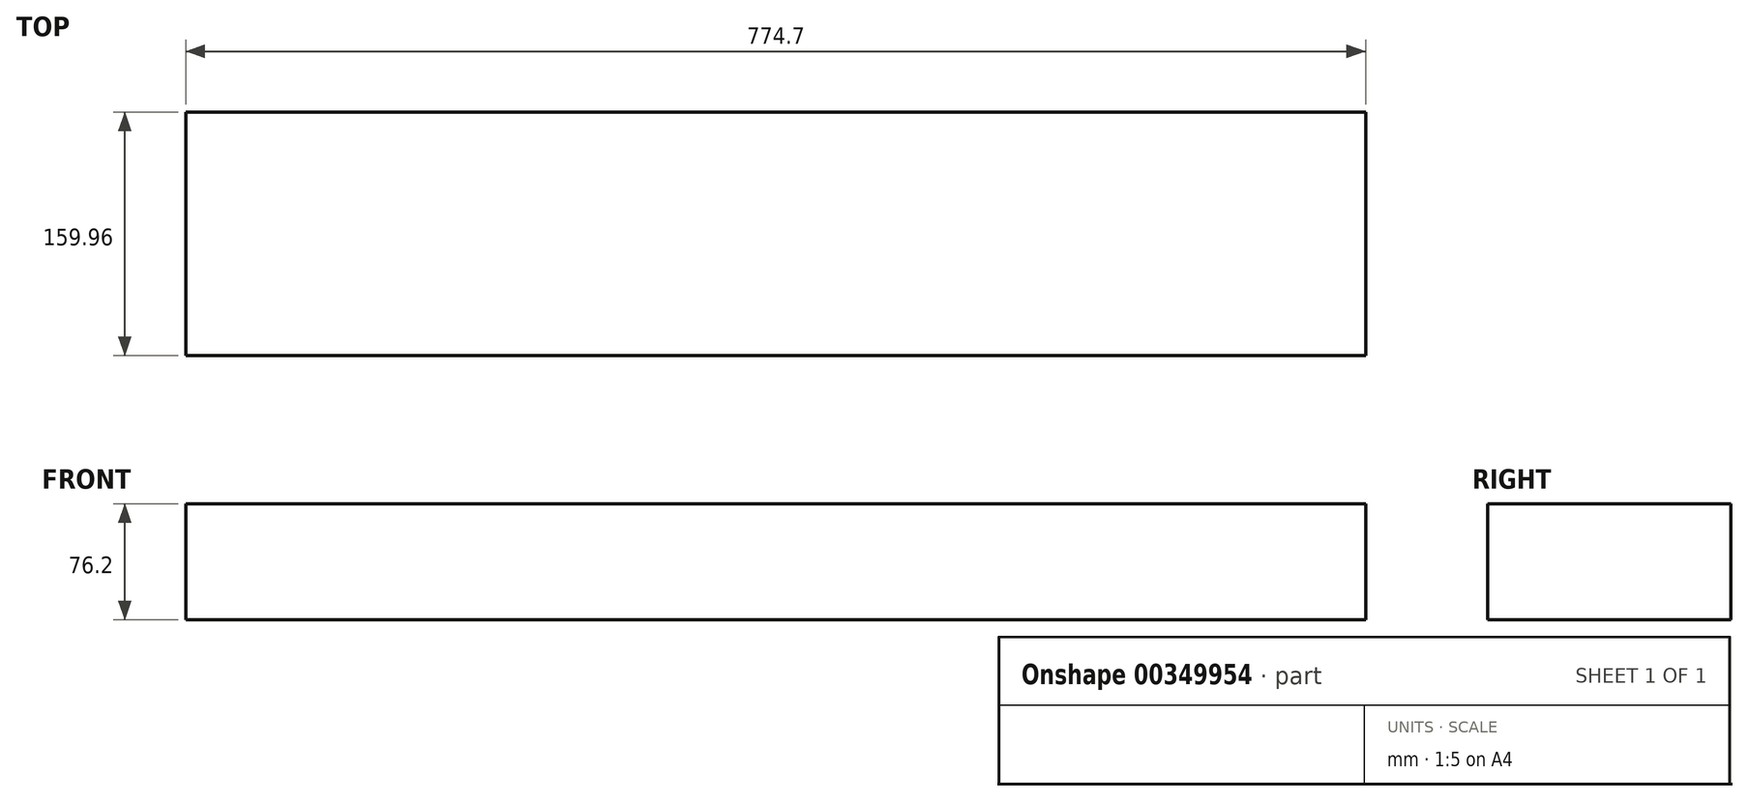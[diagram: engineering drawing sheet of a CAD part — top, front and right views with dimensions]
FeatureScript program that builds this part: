
annotation { "Feature Type Name" : "Feature", "Feature Type Description" : "" }
export const myFeature = defineFeature(function(context is Context, id is Id, definition is map)
    precondition{}
    {
        {
            var Q0;
            Q0=qCreatedBy(makeId("Top.planeOp"),FACE);
            var sketch = newSketch(context, id + "F0", { "sketchPlane" : qUnion([Q0])});
            skLineSegment(sketch, "E0.bottom", {"start": v(387.35, -73.7) * mm, "end": v(-387.35, -73.7) * mm});
            skLineSegment(sketch, "E0.top", {"start": v(387.35, 86.25) * mm, "end": v(-387.35, 86.25) * mm});
            skLineSegment(sketch, "E0.left", {"start": v(387.35, -73.7) * mm, "end": v(387.35, 86.25) * mm});
            skLineSegment(sketch, "E0.right", {"start": v(-387.35, -73.7) * mm, "end": v(-387.35, 86.25) * mm});
            skPoint(sketch, "E0.middle", {"position": v(0, 6.27) * mm});
            skSolve(sketch);
        }
        {
            var Q0;
            Q0 = qSketchRegion(id + "F0", true);
            extrude(context, id + "F1", {"entities" : qUnion([Q0]), "depth" : 76.2 * mm});
        }
    });
